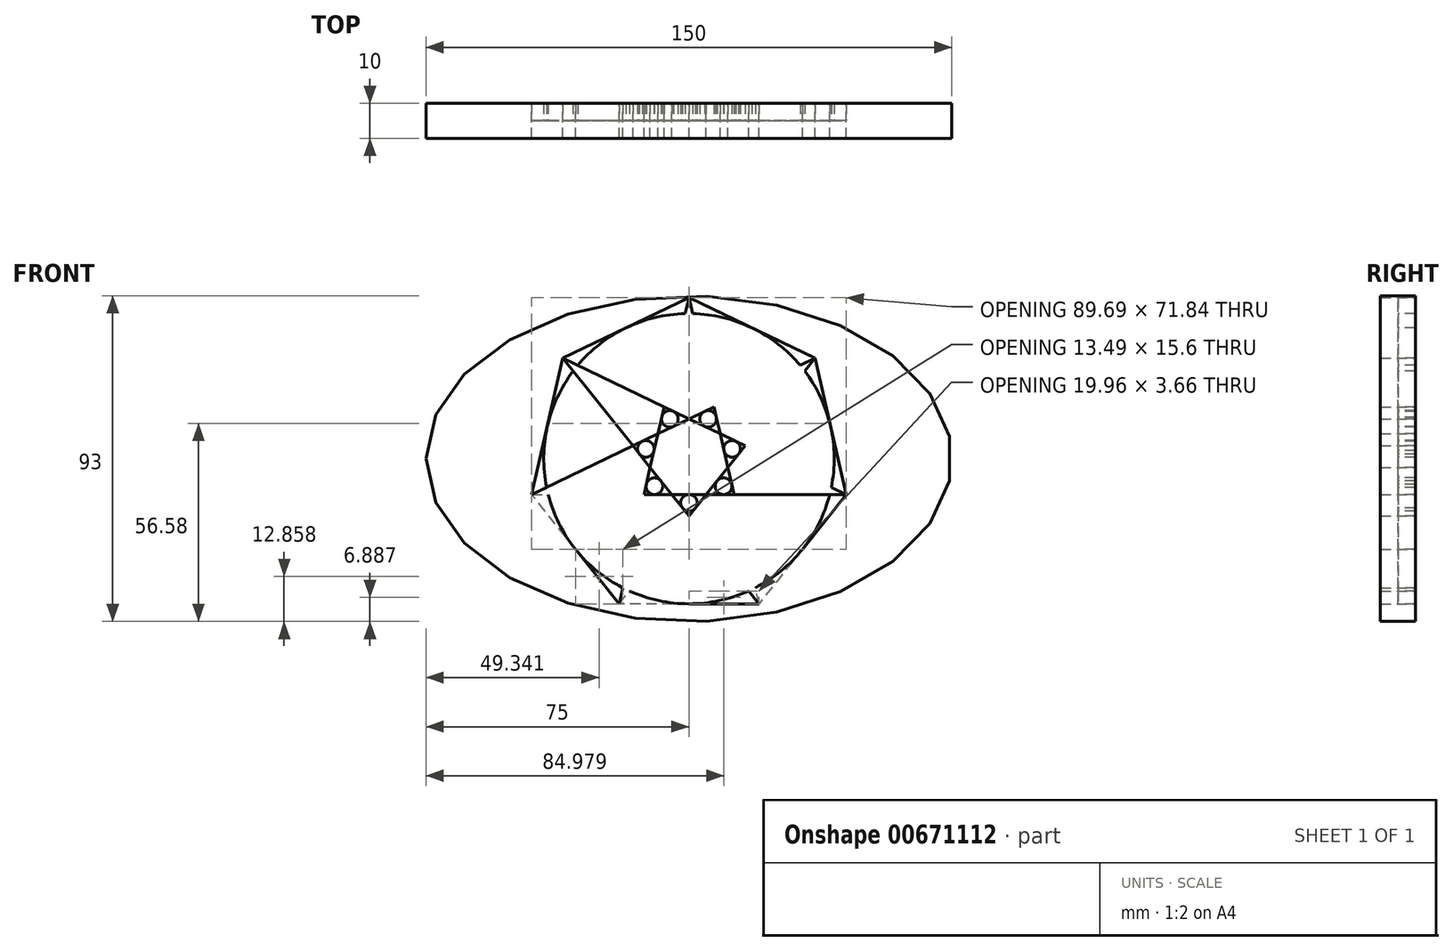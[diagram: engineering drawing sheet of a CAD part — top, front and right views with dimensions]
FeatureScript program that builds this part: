
annotation { "Feature Type Name" : "Feature", "Feature Type Description" : "" }
export const myFeature = defineFeature(function(context is Context, id is Id, definition is map)
    precondition{}
    {
        {
            var Q0;
            Q0=qCreatedBy(makeId("Front.planeOp"),FACE);
            var sketch = newSketch(context, id + "F0", { "sketchPlane" : qUnion([Q0])});
            skCircle(sketch, "E0", {"center": v(0, 0) * mm, "radius": 46 * mm});
            skEllipse(sketch, "E1", {"center": v(0, 0) * mm, "majorRadius": 75 * mm, "minorRadius": 46.5 * mm, "majorAxis": v(-1, 0)});
            skCircle(sketch, "E2.cCircle", {"center": v(0, 0) * mm, "radius": 46 * mm, "construction": true});
            skLineSegment(sketch, "E2.0", {"start": v(0, 46) * mm, "end": v(35.96, 28.68) * mm});
            skLineSegment(sketch, "E2.1", {"start": v(35.96, 28.68) * mm, "end": v(44.85, -10.24) * mm});
            skLineSegment(sketch, "E2.2", {"start": v(44.85, -10.24) * mm, "end": v(19.96, -41.44) * mm});
            skLineSegment(sketch, "E2.3", {"start": v(19.96, -41.44) * mm, "end": v(-19.96, -41.44) * mm});
            skLineSegment(sketch, "E2.4", {"start": v(-19.96, -41.44) * mm, "end": v(-44.85, -10.24) * mm});
            skLineSegment(sketch, "E2.5", {"start": v(-44.85, -10.24) * mm, "end": v(-35.96, 28.68) * mm});
            skLineSegment(sketch, "E2.6", {"start": v(-35.96, 28.68) * mm, "end": v(0, 46) * mm});
            skCircle(sketch, "E3", {"center": v(0, 0) * mm, "radius": 41.44 * mm});
            skLineSegment(sketch, "E4", {"start": v(-35.96, 28.68) * mm, "end": v(44.85, -10.24) * mm});
            skLineSegment(sketch, "E5", {"start": v(-35.96, 28.68) * mm, "end": v(19.96, -41.44) * mm});
            skLineSegment(sketch, "E6", {"start": v(19.96, -41.44) * mm, "end": v(0, 46) * mm});
            skLineSegment(sketch, "E7", {"start": v(-19.96, -41.44) * mm, "end": v(35.96, 28.68) * mm});
            skLineSegment(sketch, "E8", {"start": v(-44.85, -10.24) * mm, "end": v(44.85, -10.24) * mm});
            skLineSegment(sketch, "E9", {"start": v(0, 46) * mm, "end": v(-19.96, -41.44) * mm});
            skLineSegment(sketch, "E10", {"start": v(35.96, 28.68) * mm, "end": v(-44.85, -10.24) * mm});
            skPoint(sketch, "E11", {"position": v(-12.3, 2.8) * mm});
            skCircle(sketch, "E12", {"center": v(-12.3, 2.8) * mm, "radius": 2.37 * mm});
            skLineSegment(sketch, "E13", {"start": v(-16, 3.65) * mm, "end": v(-9.98, 2.28) * mm});
            skCircle(sketch, "E14.1.0", {"center": v(-9.86, -7.86) * mm, "radius": 2.37 * mm});
            skLineSegment(sketch, "E14.1.1", {"start": v(-12.84, -10.24) * mm, "end": v(-8, -6.38) * mm});
            skPoint(sketch, "E14.1.2", {"position": v(-9.86, -7.86) * mm});
            skCircle(sketch, "E14.2.0", {"center": v(0, -12.6) * mm, "radius": 2.37 * mm});
            skLineSegment(sketch, "E14.2.1", {"start": v(0, -16.42) * mm, "end": v(0, -10.24) * mm});
            skPoint(sketch, "E14.2.2", {"position": v(0, -12.6) * mm});
            skCircle(sketch, "E14.3.0", {"center": v(9.86, -7.86) * mm, "radius": 2.37 * mm});
            skLineSegment(sketch, "E14.3.1", {"start": v(12.84, -10.24) * mm, "end": v(8, -6.38) * mm});
            skPoint(sketch, "E14.3.2", {"position": v(9.86, -7.86) * mm});
            skCircle(sketch, "E14.4.0", {"center": v(12.3, 2.8) * mm, "radius": 2.37 * mm});
            skLineSegment(sketch, "E14.4.1", {"start": v(16, 3.65) * mm, "end": v(9.98, 2.28) * mm});
            skPoint(sketch, "E14.4.2", {"position": v(12.3, 2.8) * mm});
            skCircle(sketch, "E14.5.0", {"center": v(5.47, 11.36) * mm, "radius": 2.37 * mm});
            skLineSegment(sketch, "E14.5.1", {"start": v(7.12, 14.8) * mm, "end": v(4.44, 9.22) * mm});
            skPoint(sketch, "E14.5.2", {"position": v(5.47, 11.36) * mm});
            skCircle(sketch, "E14.6.0", {"center": v(-5.47, 11.36) * mm, "radius": 2.37 * mm});
            skLineSegment(sketch, "E14.6.1", {"start": v(-7.12, 14.8) * mm, "end": v(-4.44, 9.22) * mm});
            skPoint(sketch, "E14.6.2", {"position": v(-5.47, 11.36) * mm});
            skSolve(sketch);
        }
        {
            var Q0;
            {var subQ1=sQuery(id+"F0.wireOp",EDGE,"E4");var subQ7=sQuery(id+"F0.wireOp",EDGE,"E3");var subQ9=makeQuery(id+"F0.imprint","INTERSECT",VERTEX,{"disambiguationData":[OD(0.0)],"derivedFrom":[subQ7,subQ1]});Q0=makeQuery(id+"F0.imprint","IMPRINT",FACE,{"disambiguationData":[TD([[makeQuery(id+"F0.imprint","IMPRINT",EDGE,{"disambiguationData":[TD([[subQ9,-1.0]])],"derivedFrom":subQ7}),1.0]])]});}
            var Q1;
            {var subQ0=sQuery(id+"F0.wireOp",EDGE,"E4");var subQ1=sQuery(id+"F0.wireOp",EDGE,"E3");var subQ2=makeQuery(id+"F0.imprint","INTERSECT",VERTEX,{"disambiguationData":[OD(0.0)],"derivedFrom":[subQ1,subQ0]});Q1=makeQuery(id+"F0.imprint","IMPRINT",FACE,{"disambiguationData":[TD([[makeQuery(id+"F0.imprint","IMPRINT",EDGE,{"disambiguationData":[TD([[subQ2,-1.0]])],"derivedFrom":subQ1}),-1.0]])]});}
            var Q2;
            {var subQ3=sQuery(id+"F0.wireOp",EDGE,"E3");var subQ5=sQuery(id+"F0.wireOp",EDGE,"E10");var subQ6=makeQuery(id+"F0.imprint","INTERSECT",VERTEX,{"disambiguationData":[OD(1.0)],"derivedFrom":[subQ3,subQ5]});Q2=makeQuery(id+"F0.imprint","IMPRINT",FACE,{"disambiguationData":[TD([[makeQuery(id+"F0.imprint","IMPRINT",EDGE,{"disambiguationData":[TD([[subQ6,-1.0]])],"derivedFrom":subQ3}),1.0]])]});}
            var Q3;
            {var subQ0=sQuery(id+"F0.wireOp",EDGE,"E10");var subQ1=sQuery(id+"F0.wireOp",EDGE,"E3");var subQ2=makeQuery(id+"F0.imprint","INTERSECT",VERTEX,{"disambiguationData":[OD(1.0)],"derivedFrom":[subQ1,subQ0]});Q3=makeQuery(id+"F0.imprint","IMPRINT",FACE,{"disambiguationData":[TD([[makeQuery(id+"F0.imprint","IMPRINT",EDGE,{"disambiguationData":[TD([[subQ2,-1.0]])],"derivedFrom":subQ1}),-1.0]])]});}
            var Q4;
            {var subQ0=sQuery(id+"F0.wireOp",EDGE,"E9");var subQ7=sQuery(id+"F0.wireOp",EDGE,"E3");var subQ9=makeQuery(id+"F0.imprint","INTERSECT",VERTEX,{"disambiguationData":[OD(1.0)],"derivedFrom":[subQ7,subQ0]});Q4=makeQuery(id+"F0.imprint","IMPRINT",FACE,{"disambiguationData":[TD([[makeQuery(id+"F0.imprint","IMPRINT",EDGE,{"disambiguationData":[TD([[subQ9,-1.0]])],"derivedFrom":subQ7}),1.0]])]});}
            var Q5;
            {var subQ0=sQuery(id+"F0.wireOp",EDGE,"E9");var subQ1=sQuery(id+"F0.wireOp",EDGE,"E3");var subQ2=makeQuery(id+"F0.imprint","INTERSECT",VERTEX,{"disambiguationData":[OD(1.0)],"derivedFrom":[subQ1,subQ0]});Q5=makeQuery(id+"F0.imprint","IMPRINT",FACE,{"disambiguationData":[TD([[makeQuery(id+"F0.imprint","IMPRINT",EDGE,{"disambiguationData":[TD([[subQ2,-1.0]])],"derivedFrom":subQ1}),-1.0]])]});}
            var Q6;
            {var subQ1=sQuery(id+"F0.wireOp",EDGE,"E5");var subQ7=sQuery(id+"F0.wireOp",EDGE,"E3");var subQ9=makeQuery(id+"F0.imprint","INTERSECT",VERTEX,{"disambiguationData":[OD(1.0)],"derivedFrom":[subQ7,subQ1]});Q6=makeQuery(id+"F0.imprint","IMPRINT",FACE,{"disambiguationData":[TD([[makeQuery(id+"F0.imprint","IMPRINT",EDGE,{"disambiguationData":[TD([[subQ9,-1.0]])],"derivedFrom":subQ7}),1.0]])]});}
            var Q7;
            {var subQ0=sQuery(id+"F0.wireOp",EDGE,"E5");var subQ1=sQuery(id+"F0.wireOp",EDGE,"E3");var subQ2=makeQuery(id+"F0.imprint","INTERSECT",VERTEX,{"disambiguationData":[OD(1.0)],"derivedFrom":[subQ1,subQ0]});Q7=makeQuery(id+"F0.imprint","IMPRINT",FACE,{"disambiguationData":[TD([[makeQuery(id+"F0.imprint","IMPRINT",EDGE,{"disambiguationData":[TD([[subQ2,-1.0]])],"derivedFrom":subQ1}),-1.0]])]});}
            var Q8;
            {var subQ5=sQuery(id+"F0.wireOp",EDGE,"E8");var subQ7=sQuery(id+"F0.wireOp",EDGE,"E3");var subQ9=makeQuery(id+"F0.imprint","INTERSECT",VERTEX,{"disambiguationData":[OD(1.0)],"derivedFrom":[subQ7,subQ5]});Q8=makeQuery(id+"F0.imprint","IMPRINT",FACE,{"disambiguationData":[TD([[makeQuery(id+"F0.imprint","IMPRINT",EDGE,{"disambiguationData":[TD([[subQ9,-1.0]])],"derivedFrom":subQ7}),1.0]])]});}
            var Q9;
            {var subQ0=sQuery(id+"F0.wireOp",EDGE,"E8");var subQ1=sQuery(id+"F0.wireOp",EDGE,"E3");var subQ2=makeQuery(id+"F0.imprint","INTERSECT",VERTEX,{"disambiguationData":[OD(1.0)],"derivedFrom":[subQ1,subQ0]});Q9=makeQuery(id+"F0.imprint","IMPRINT",FACE,{"disambiguationData":[TD([[makeQuery(id+"F0.imprint","IMPRINT",EDGE,{"disambiguationData":[TD([[subQ2,-1.0]])],"derivedFrom":subQ1}),-1.0]])]});}
            var Q10;
            {var subQ5=sQuery(id+"F0.wireOp",EDGE,"E7");var subQ7=sQuery(id+"F0.wireOp",EDGE,"E3");var subQ8=makeQuery(id+"F0.imprint","INTERSECT",VERTEX,{"disambiguationData":[OD(0.0)],"derivedFrom":[subQ7,subQ5]});Q10=makeQuery(id+"F0.imprint","IMPRINT",FACE,{"disambiguationData":[TD([[makeQuery(id+"F0.imprint","IMPRINT",EDGE,{"disambiguationData":[TD([[subQ8,-1.0]])],"derivedFrom":subQ7}),1.0]])]});}
            var Q11;
            {var subQ0=sQuery(id+"F0.wireOp",EDGE,"E7");var subQ1=sQuery(id+"F0.wireOp",EDGE,"E3");var subQ2=makeQuery(id+"F0.imprint","INTERSECT",VERTEX,{"disambiguationData":[OD(0.0)],"derivedFrom":[subQ1,subQ0]});Q11=makeQuery(id+"F0.imprint","IMPRINT",FACE,{"disambiguationData":[TD([[makeQuery(id+"F0.imprint","IMPRINT",EDGE,{"disambiguationData":[TD([[subQ2,-1.0]])],"derivedFrom":subQ1}),-1.0]])]});}
            var Q12;
            {var subQ3=sQuery(id+"F0.wireOp",EDGE,"E3");var subQ6=sQuery(id+"F0.wireOp",EDGE,"E6");var subQ8=makeQuery(id+"F0.imprint","INTERSECT",VERTEX,{"disambiguationData":[OD(0.0)],"derivedFrom":[subQ3,subQ6]});Q12=makeQuery(id+"F0.imprint","IMPRINT",FACE,{"disambiguationData":[TD([[makeQuery(id+"F0.imprint","IMPRINT",EDGE,{"disambiguationData":[TD([[subQ8,-1.0]])],"derivedFrom":subQ3}),1.0]])]});}
            var Q13;
            {var subQ0=sQuery(id+"F0.wireOp",EDGE,"E6");var subQ1=sQuery(id+"F0.wireOp",EDGE,"E3");var subQ2=makeQuery(id+"F0.imprint","INTERSECT",VERTEX,{"disambiguationData":[OD(0.0)],"derivedFrom":[subQ1,subQ0]});Q13=makeQuery(id+"F0.imprint","IMPRINT",FACE,{"disambiguationData":[TD([[makeQuery(id+"F0.imprint","IMPRINT",EDGE,{"disambiguationData":[TD([[subQ2,-1.0]])],"derivedFrom":subQ1}),-1.0]])]});}
            var Q14;
            {var subQ0=sQuery(id+"F0.wireOp",EDGE,"3fb7257f-58bd-4f18-b406-dab5ca3c946f");Q14=makeQuery(id+"F0.imprint","IMPRINT",FACE,{"disambiguationData":[TD([[makeQuery(id+"F0.imprint","IMPRINT",EDGE,{"derivedFrom":subQ0}),1.0]])]});}
            var Q15;
            {var subQ0=sQuery(id+"F0.wireOp",EDGE,"b29785f3-1675-4353-98de-94516835d5aa.5.1");Q15=makeQuery(id+"F0.imprint","IMPRINT",FACE,{"disambiguationData":[TD([[makeQuery(id+"F0.imprint","IMPRINT",EDGE,{"derivedFrom":subQ0}),-1.0]])]});}
            var Q16;
            {var subQ4=sQuery(id+"F0.wireOp",EDGE,"b29785f3-1675-4353-98de-94516835d5aa.4.1");Q16=makeQuery(id+"F0.imprint","IMPRINT",FACE,{"disambiguationData":[TD([[makeQuery(id+"F0.imprint","IMPRINT",EDGE,{"derivedFrom":subQ4}),-1.0]])]});}
            var Q17;
            {var subQ4=sQuery(id+"F0.wireOp",EDGE,"b29785f3-1675-4353-98de-94516835d5aa.3.1");Q17=makeQuery(id+"F0.imprint","IMPRINT",FACE,{"disambiguationData":[TD([[makeQuery(id+"F0.imprint","IMPRINT",EDGE,{"derivedFrom":subQ4}),-1.0]])]});}
            var Q18;
            {var subQ4=sQuery(id+"F0.wireOp",EDGE,"b29785f3-1675-4353-98de-94516835d5aa.2.1");Q18=makeQuery(id+"F0.imprint","IMPRINT",FACE,{"disambiguationData":[TD([[makeQuery(id+"F0.imprint","IMPRINT",EDGE,{"derivedFrom":subQ4}),-1.0]])]});}
            var Q19;
            {var subQ0=sQuery(id+"F0.wireOp",EDGE,"b29785f3-1675-4353-98de-94516835d5aa.1.1");Q19=makeQuery(id+"F0.imprint","IMPRINT",FACE,{"disambiguationData":[TD([[makeQuery(id+"F0.imprint","IMPRINT",EDGE,{"derivedFrom":subQ0}),-1.0]])]});}
            var Q20;
            {var subQ4=sQuery(id+"F0.wireOp",EDGE,"3fb7257f-58bd-4f18-b406-dab5ca3c946f");Q20=makeQuery(id+"F0.imprint","IMPRINT",FACE,{"disambiguationData":[TD([[makeQuery(id+"F0.imprint","IMPRINT",EDGE,{"derivedFrom":subQ4}),-1.0]])]});}
            var Q21;
            Q21=makeQuery(id+"F0.imprint","IMPRINT",FACE,{"disambiguationData":[TD([[makeQuery(id+"F0.imprint","IMPRINT",EDGE,{"derivedFrom":sQuery(id+"F0.wireOp",EDGE,"E1")}),1.0]])]});
            var Q22;
            {var subQ0=sQuery(id+"F0.wireOp",EDGE,"E2.3");var subQ4=makeQuery(id+"F0.imprint","INTERSECT",VERTEX,{"derivedFrom":[subQ0,sQuery(id+"F0.wireOp",EDGE,"E3")]});Q22=makeQuery(id+"F0.imprint","IMPRINT",FACE,{"disambiguationData":[TD([[makeQuery(id+"F0.imprint","IMPRINT",EDGE,{"disambiguationData":[TD([[subQ4,1.0]])],"derivedFrom":subQ0}),1.0]])]});}
            var Q23;
            {var subQ0=sQuery(id+"F0.wireOp",EDGE,"E2.4");var subQ4=makeQuery(id+"F0.imprint","INTERSECT",VERTEX,{"derivedFrom":[subQ0,sQuery(id+"F0.wireOp",EDGE,"E3")]});Q23=makeQuery(id+"F0.imprint","IMPRINT",FACE,{"disambiguationData":[TD([[makeQuery(id+"F0.imprint","IMPRINT",EDGE,{"disambiguationData":[TD([[subQ4,1.0]])],"derivedFrom":subQ0}),1.0]])]});}
            var Q24;
            {var subQ0=sQuery(id+"F0.wireOp",EDGE,"E2.5");var subQ4=makeQuery(id+"F0.imprint","INTERSECT",VERTEX,{"derivedFrom":[subQ0,sQuery(id+"F0.wireOp",EDGE,"E3")]});Q24=makeQuery(id+"F0.imprint","IMPRINT",FACE,{"disambiguationData":[TD([[makeQuery(id+"F0.imprint","IMPRINT",EDGE,{"disambiguationData":[TD([[subQ4,1.0]])],"derivedFrom":subQ0}),1.0]])]});}
            var Q25;
            {var subQ0=sQuery(id+"F0.wireOp",EDGE,"E2.6");var subQ4=makeQuery(id+"F0.imprint","INTERSECT",VERTEX,{"derivedFrom":[subQ0,sQuery(id+"F0.wireOp",EDGE,"E3")]});Q25=makeQuery(id+"F0.imprint","IMPRINT",FACE,{"disambiguationData":[TD([[makeQuery(id+"F0.imprint","IMPRINT",EDGE,{"disambiguationData":[TD([[subQ4,1.0]])],"derivedFrom":subQ0}),1.0]])]});}
            var Q26;
            {var subQ0=sQuery(id+"F0.wireOp",EDGE,"E2.0");var subQ4=makeQuery(id+"F0.imprint","INTERSECT",VERTEX,{"derivedFrom":[subQ0,sQuery(id+"F0.wireOp",EDGE,"E3")]});Q26=makeQuery(id+"F0.imprint","IMPRINT",FACE,{"disambiguationData":[TD([[makeQuery(id+"F0.imprint","IMPRINT",EDGE,{"disambiguationData":[TD([[subQ4,1.0]])],"derivedFrom":subQ0}),1.0]])]});}
            var Q27;
            {var subQ0=sQuery(id+"F0.wireOp",EDGE,"E2.1");var subQ4=makeQuery(id+"F0.imprint","INTERSECT",VERTEX,{"derivedFrom":[subQ0,sQuery(id+"F0.wireOp",EDGE,"E3")]});Q27=makeQuery(id+"F0.imprint","IMPRINT",FACE,{"disambiguationData":[TD([[makeQuery(id+"F0.imprint","IMPRINT",EDGE,{"disambiguationData":[TD([[subQ4,1.0]])],"derivedFrom":subQ0}),1.0]])]});}
            var Q28;
            {var subQ0=sQuery(id+"F0.wireOp",EDGE,"E2.2");var subQ4=makeQuery(id+"F0.imprint","INTERSECT",VERTEX,{"derivedFrom":[subQ0,sQuery(id+"F0.wireOp",EDGE,"E3")]});Q28=makeQuery(id+"F0.imprint","IMPRINT",FACE,{"disambiguationData":[TD([[makeQuery(id+"F0.imprint","IMPRINT",EDGE,{"disambiguationData":[TD([[subQ4,1.0]])],"derivedFrom":subQ0}),1.0]])]});}
            var Q29;
            {var subQ10=sQuery(id+"F0.wireOp",EDGE,"E4");var subQ16=sQuery(id+"F0.wireOp",EDGE,"E10");var subQ17=makeQuery(id+"F0.imprint","INTERSECT",VERTEX,{"derivedFrom":[subQ10,subQ16]});Q29=makeQuery(id+"F0.imprint","IMPRINT",FACE,{"disambiguationData":[TD([[makeQuery(id+"F0.imprint","IMPRINT",EDGE,{"disambiguationData":[TD([[subQ17,-1.0]])],"derivedFrom":subQ10}),-1.0]])]});}
            extrude(context, id + "F1", {"entities" : qUnion([Q0, Q1, Q2, Q3, Q4, Q5, Q6, Q7, Q8, Q9, Q10, Q11, Q12, Q13, Q14, Q15, Q16, Q17, Q18, Q19, Q20, Q21, Q22, Q23, Q24, Q25, Q26, Q27, Q28, Q29]), "endBound" : BoundingType.SYMMETRIC, "depth" : 10 * mm, "offsetDistance" : 25 * mm});
        }
        {
            var Q0;
            {var subQ1=sQuery(id+"F0.wireOp",EDGE,"E2.5");var subQ3=sQuery(id+"F0.wireOp",EDGE,"E3");var subQ4=makeQuery(id+"F0.imprint","INTERSECT",VERTEX,{"derivedFrom":[subQ1,subQ3]});Q0=makeQuery(id+"F0.imprint","IMPRINT",FACE,{"disambiguationData":[TD([[makeQuery(id+"F0.imprint","IMPRINT",EDGE,{"disambiguationData":[TD([[subQ4,1.0]])],"derivedFrom":subQ3}),-1.0]])]});}
            var Q1;
            {var subQ1=sQuery(id+"F0.wireOp",EDGE,"E2.6");var subQ3=sQuery(id+"F0.wireOp",EDGE,"E3");var subQ4=makeQuery(id+"F0.imprint","INTERSECT",VERTEX,{"derivedFrom":[subQ1,subQ3]});Q1=makeQuery(id+"F0.imprint","IMPRINT",FACE,{"disambiguationData":[TD([[makeQuery(id+"F0.imprint","IMPRINT",EDGE,{"disambiguationData":[TD([[subQ4,-1.0]])],"derivedFrom":subQ3}),-1.0]])]});}
            var Q2;
            {var subQ1=sQuery(id+"F0.wireOp",EDGE,"E2.6");var subQ3=sQuery(id+"F0.wireOp",EDGE,"E3");var subQ4=makeQuery(id+"F0.imprint","INTERSECT",VERTEX,{"derivedFrom":[subQ1,subQ3]});Q2=makeQuery(id+"F0.imprint","IMPRINT",FACE,{"disambiguationData":[TD([[makeQuery(id+"F0.imprint","IMPRINT",EDGE,{"disambiguationData":[TD([[subQ4,1.0]])],"derivedFrom":subQ3}),-1.0]])]});}
            var Q3;
            {var subQ1=sQuery(id+"F0.wireOp",EDGE,"E2.0");var subQ3=sQuery(id+"F0.wireOp",EDGE,"E3");var subQ4=makeQuery(id+"F0.imprint","INTERSECT",VERTEX,{"derivedFrom":[subQ1,subQ3]});Q3=makeQuery(id+"F0.imprint","IMPRINT",FACE,{"disambiguationData":[TD([[makeQuery(id+"F0.imprint","IMPRINT",EDGE,{"disambiguationData":[TD([[subQ4,-1.0]])],"derivedFrom":subQ3}),-1.0]])]});}
            var Q4;
            {var subQ1=sQuery(id+"F0.wireOp",EDGE,"E2.0");var subQ3=sQuery(id+"F0.wireOp",EDGE,"E3");var subQ4=makeQuery(id+"F0.imprint","INTERSECT",VERTEX,{"derivedFrom":[subQ1,subQ3]});Q4=makeQuery(id+"F0.imprint","IMPRINT",FACE,{"disambiguationData":[TD([[makeQuery(id+"F0.imprint","IMPRINT",EDGE,{"disambiguationData":[TD([[subQ4,1.0]])],"derivedFrom":subQ3}),-1.0]])]});}
            var Q5;
            {var subQ1=sQuery(id+"F0.wireOp",EDGE,"E2.1");var subQ3=sQuery(id+"F0.wireOp",EDGE,"E3");var subQ4=makeQuery(id+"F0.imprint","INTERSECT",VERTEX,{"derivedFrom":[subQ1,subQ3]});Q5=makeQuery(id+"F0.imprint","IMPRINT",FACE,{"disambiguationData":[TD([[makeQuery(id+"F0.imprint","IMPRINT",EDGE,{"disambiguationData":[TD([[subQ4,-1.0]])],"derivedFrom":subQ3}),-1.0]])]});}
            var Q6;
            {var subQ1=sQuery(id+"F0.wireOp",EDGE,"E2.1");var subQ3=sQuery(id+"F0.wireOp",EDGE,"E3");var subQ4=makeQuery(id+"F0.imprint","INTERSECT",VERTEX,{"derivedFrom":[subQ1,subQ3]});Q6=makeQuery(id+"F0.imprint","IMPRINT",FACE,{"disambiguationData":[TD([[makeQuery(id+"F0.imprint","IMPRINT",EDGE,{"disambiguationData":[TD([[subQ4,1.0]])],"derivedFrom":subQ3}),-1.0]])]});}
            var Q7;
            {var subQ1=sQuery(id+"F0.wireOp",EDGE,"E2.2");var subQ3=sQuery(id+"F0.wireOp",EDGE,"E3");var subQ4=makeQuery(id+"F0.imprint","INTERSECT",VERTEX,{"derivedFrom":[subQ1,subQ3]});Q7=makeQuery(id+"F0.imprint","IMPRINT",FACE,{"disambiguationData":[TD([[makeQuery(id+"F0.imprint","IMPRINT",EDGE,{"disambiguationData":[TD([[subQ4,-1.0]])],"derivedFrom":subQ3}),-1.0]])]});}
            var Q8;
            {var subQ1=sQuery(id+"F0.wireOp",EDGE,"E2.2");var subQ3=sQuery(id+"F0.wireOp",EDGE,"E3");var subQ4=makeQuery(id+"F0.imprint","INTERSECT",VERTEX,{"derivedFrom":[subQ1,subQ3]});Q8=makeQuery(id+"F0.imprint","IMPRINT",FACE,{"disambiguationData":[TD([[makeQuery(id+"F0.imprint","IMPRINT",EDGE,{"disambiguationData":[TD([[subQ4,1.0]])],"derivedFrom":subQ3}),-1.0]])]});}
            var Q9;
            {var subQ1=sQuery(id+"F0.wireOp",EDGE,"E2.3");var subQ3=sQuery(id+"F0.wireOp",EDGE,"E3");var subQ4=makeQuery(id+"F0.imprint","INTERSECT",VERTEX,{"derivedFrom":[subQ1,subQ3]});Q9=makeQuery(id+"F0.imprint","IMPRINT",FACE,{"disambiguationData":[TD([[makeQuery(id+"F0.imprint","IMPRINT",EDGE,{"disambiguationData":[TD([[subQ4,-1.0]])],"derivedFrom":subQ3}),-1.0]])]});}
            var Q10;
            {var subQ1=sQuery(id+"F0.wireOp",EDGE,"E2.3");var subQ3=sQuery(id+"F0.wireOp",EDGE,"E3");var subQ4=makeQuery(id+"F0.imprint","INTERSECT",VERTEX,{"derivedFrom":[subQ1,subQ3]});Q10=makeQuery(id+"F0.imprint","IMPRINT",FACE,{"disambiguationData":[TD([[makeQuery(id+"F0.imprint","IMPRINT",EDGE,{"disambiguationData":[TD([[subQ4,1.0]])],"derivedFrom":subQ3}),-1.0]])]});}
            var Q11;
            {var subQ1=sQuery(id+"F0.wireOp",EDGE,"E2.4");var subQ3=sQuery(id+"F0.wireOp",EDGE,"E3");var subQ4=makeQuery(id+"F0.imprint","INTERSECT",VERTEX,{"derivedFrom":[subQ1,subQ3]});Q11=makeQuery(id+"F0.imprint","IMPRINT",FACE,{"disambiguationData":[TD([[makeQuery(id+"F0.imprint","IMPRINT",EDGE,{"disambiguationData":[TD([[subQ4,-1.0]])],"derivedFrom":subQ3}),-1.0]])]});}
            var Q12;
            {var subQ1=sQuery(id+"F0.wireOp",EDGE,"E2.4");var subQ3=sQuery(id+"F0.wireOp",EDGE,"E3");var subQ4=makeQuery(id+"F0.imprint","INTERSECT",VERTEX,{"derivedFrom":[subQ1,subQ3]});Q12=makeQuery(id+"F0.imprint","IMPRINT",FACE,{"disambiguationData":[TD([[makeQuery(id+"F0.imprint","IMPRINT",EDGE,{"disambiguationData":[TD([[subQ4,1.0]])],"derivedFrom":subQ3}),-1.0]])]});}
            var Q13;
            {var subQ1=sQuery(id+"F0.wireOp",EDGE,"E2.5");var subQ3=sQuery(id+"F0.wireOp",EDGE,"E3");var subQ4=makeQuery(id+"F0.imprint","INTERSECT",VERTEX,{"derivedFrom":[subQ1,subQ3]});Q13=makeQuery(id+"F0.imprint","IMPRINT",FACE,{"disambiguationData":[TD([[makeQuery(id+"F0.imprint","IMPRINT",EDGE,{"disambiguationData":[TD([[subQ4,-1.0]])],"derivedFrom":subQ3}),-1.0]])]});}
            var Q14;
            {var subQ0=sQuery(id+"F0.wireOp",EDGE,"E14.6.0");var subQ1=sQuery(id+"F0.wireOp",EDGE,"E9");var subQ2=makeQuery(id+"F0.imprint","INTERSECT",VERTEX,{"derivedFrom":[subQ1,subQ0]});Q14=makeQuery(id+"F0.imprint","IMPRINT",FACE,{"disambiguationData":[TD([[makeQuery(id+"F0.imprint","IMPRINT",EDGE,{"disambiguationData":[TD([[subQ2,-1.0]])],"derivedFrom":subQ1}),1.0]])]});}
            var Q15;
            {var subQ1=sQuery(id+"F0.wireOp",EDGE,"E9");var subQ3=sQuery(id+"F0.wireOp",EDGE,"E14.6.0");var subQ4=makeQuery(id+"F0.imprint","INTERSECT",VERTEX,{"derivedFrom":[subQ1,subQ3]});Q15=makeQuery(id+"F0.imprint","IMPRINT",FACE,{"disambiguationData":[TD([[makeQuery(id+"F0.imprint","IMPRINT",EDGE,{"disambiguationData":[TD([[subQ4,1.0]])],"derivedFrom":subQ3}),-1.0]])]});}
            var Q16;
            {var subQ1=sQuery(id+"F0.wireOp",EDGE,"E4");var subQ3=sQuery(id+"F0.wireOp",EDGE,"E14.6.0");var subQ4=makeQuery(id+"F0.imprint","INTERSECT",VERTEX,{"derivedFrom":[subQ1,subQ3]});Q16=makeQuery(id+"F0.imprint","IMPRINT",FACE,{"disambiguationData":[TD([[makeQuery(id+"F0.imprint","IMPRINT",EDGE,{"disambiguationData":[TD([[subQ4,-1.0]])],"derivedFrom":subQ3}),-1.0]])]});}
            var Q17;
            {var subQ0=sQuery(id+"F0.wireOp",EDGE,"E14.6.0");var subQ1=sQuery(id+"F0.wireOp",EDGE,"E4");var subQ2=makeQuery(id+"F0.imprint","INTERSECT",VERTEX,{"derivedFrom":[subQ1,subQ0]});Q17=makeQuery(id+"F0.imprint","IMPRINT",FACE,{"disambiguationData":[TD([[makeQuery(id+"F0.imprint","IMPRINT",EDGE,{"disambiguationData":[TD([[subQ2,-1.0]])],"derivedFrom":subQ1}),-1.0]])]});}
            var Q18;
            {var subQ1=sQuery(id+"F0.wireOp",EDGE,"E6");var subQ3=sQuery(id+"F0.wireOp",EDGE,"E14.5.0");var subQ4=makeQuery(id+"F0.imprint","INTERSECT",VERTEX,{"derivedFrom":[subQ1,subQ3]});Q18=makeQuery(id+"F0.imprint","IMPRINT",FACE,{"disambiguationData":[TD([[makeQuery(id+"F0.imprint","IMPRINT",EDGE,{"disambiguationData":[TD([[subQ4,-1.0]])],"derivedFrom":subQ3}),-1.0]])]});}
            var Q19;
            {var subQ1=sQuery(id+"F0.wireOp",EDGE,"E4");var subQ3=sQuery(id+"F0.wireOp",EDGE,"E6");var subQ4=makeQuery(id+"F0.imprint","INTERSECT",VERTEX,{"derivedFrom":[subQ1,subQ3]});Q19=makeQuery(id+"F0.imprint","IMPRINT",FACE,{"disambiguationData":[TD([[makeQuery(id+"F0.imprint","IMPRINT",EDGE,{"disambiguationData":[TD([[subQ4,-1.0]])],"derivedFrom":subQ3}),1.0]])]});}
            var Q20;
            {var subQ0=sQuery(id+"F0.wireOp",EDGE,"E6");var subQ1=sQuery(id+"F0.wireOp",EDGE,"E4");var subQ2=makeQuery(id+"F0.imprint","INTERSECT",VERTEX,{"derivedFrom":[subQ1,subQ0]});Q20=makeQuery(id+"F0.imprint","IMPRINT",FACE,{"disambiguationData":[TD([[makeQuery(id+"F0.imprint","IMPRINT",EDGE,{"disambiguationData":[TD([[subQ2,-1.0]])],"derivedFrom":subQ1}),-1.0]])]});}
            var Q21;
            {var subQ1=sQuery(id+"F0.wireOp",EDGE,"E4");var subQ3=sQuery(id+"F0.wireOp",EDGE,"E10");var subQ4=makeQuery(id+"F0.imprint","INTERSECT",VERTEX,{"derivedFrom":[subQ1,subQ3]});Q21=makeQuery(id+"F0.imprint","IMPRINT",FACE,{"disambiguationData":[TD([[makeQuery(id+"F0.imprint","IMPRINT",EDGE,{"disambiguationData":[TD([[subQ4,1.0]])],"derivedFrom":subQ3}),1.0]])]});}
            var Q22;
            {var subQ1=sQuery(id+"F0.wireOp",EDGE,"E10");var subQ3=sQuery(id+"F0.wireOp",EDGE,"E14.5.0");var subQ4=makeQuery(id+"F0.imprint","INTERSECT",VERTEX,{"derivedFrom":[subQ1,subQ3]});Q22=makeQuery(id+"F0.imprint","IMPRINT",FACE,{"disambiguationData":[TD([[makeQuery(id+"F0.imprint","IMPRINT",EDGE,{"disambiguationData":[TD([[subQ4,1.0]])],"derivedFrom":subQ3}),-1.0]])]});}
            var Q23;
            {var subQ1=sQuery(id+"F0.wireOp",EDGE,"E4");var subQ3=sQuery(id+"F0.wireOp",EDGE,"E14.4.0");var subQ4=makeQuery(id+"F0.imprint","INTERSECT",VERTEX,{"derivedFrom":[subQ1,subQ3]});Q23=makeQuery(id+"F0.imprint","IMPRINT",FACE,{"disambiguationData":[TD([[makeQuery(id+"F0.imprint","IMPRINT",EDGE,{"disambiguationData":[TD([[subQ4,1.0]])],"derivedFrom":subQ3}),-1.0]])]});}
            var Q24;
            {var subQ1=sQuery(id+"F0.wireOp",EDGE,"E7");var subQ3=sQuery(id+"F0.wireOp",EDGE,"E14.4.0");var subQ4=makeQuery(id+"F0.imprint","INTERSECT",VERTEX,{"derivedFrom":[subQ1,subQ3]});Q24=makeQuery(id+"F0.imprint","IMPRINT",FACE,{"disambiguationData":[TD([[makeQuery(id+"F0.imprint","IMPRINT",EDGE,{"disambiguationData":[TD([[subQ4,-1.0]])],"derivedFrom":subQ3}),-1.0]])]});}
            var Q25;
            {var subQ1=sQuery(id+"F0.wireOp",EDGE,"E6");var subQ3=sQuery(id+"F0.wireOp",EDGE,"E7");var subQ4=makeQuery(id+"F0.imprint","INTERSECT",VERTEX,{"derivedFrom":[subQ1,subQ3]});Q25=makeQuery(id+"F0.imprint","IMPRINT",FACE,{"disambiguationData":[TD([[makeQuery(id+"F0.imprint","IMPRINT",EDGE,{"disambiguationData":[TD([[subQ4,-1.0]])],"derivedFrom":subQ3}),1.0]])]});}
            var Q26;
            {var subQ0=sQuery(id+"F0.wireOp",EDGE,"E14.3.0");var subQ1=sQuery(id+"F0.wireOp",EDGE,"E6");var subQ2=makeQuery(id+"F0.imprint","INTERSECT",VERTEX,{"derivedFrom":[subQ1,subQ0]});Q26=makeQuery(id+"F0.imprint","IMPRINT",FACE,{"disambiguationData":[TD([[makeQuery(id+"F0.imprint","IMPRINT",EDGE,{"disambiguationData":[TD([[subQ2,-1.0]])],"derivedFrom":subQ1}),1.0]])]});}
            var Q27;
            {var subQ1=sQuery(id+"F0.wireOp",EDGE,"E6");var subQ3=sQuery(id+"F0.wireOp",EDGE,"E14.3.0");var subQ4=makeQuery(id+"F0.imprint","INTERSECT",VERTEX,{"derivedFrom":[subQ1,subQ3]});Q27=makeQuery(id+"F0.imprint","IMPRINT",FACE,{"disambiguationData":[TD([[makeQuery(id+"F0.imprint","IMPRINT",EDGE,{"disambiguationData":[TD([[subQ4,1.0]])],"derivedFrom":subQ3}),-1.0]])]});}
            var Q28;
            {var subQ1=sQuery(id+"F0.wireOp",EDGE,"E8");var subQ3=sQuery(id+"F0.wireOp",EDGE,"E14.3.0");var subQ4=makeQuery(id+"F0.imprint","INTERSECT",VERTEX,{"derivedFrom":[subQ1,subQ3]});Q28=makeQuery(id+"F0.imprint","IMPRINT",FACE,{"disambiguationData":[TD([[makeQuery(id+"F0.imprint","IMPRINT",EDGE,{"disambiguationData":[TD([[subQ4,-1.0]])],"derivedFrom":subQ3}),-1.0]])]});}
            var Q29;
            {var subQ1=sQuery(id+"F0.wireOp",EDGE,"E7");var subQ3=sQuery(id+"F0.wireOp",EDGE,"E8");var subQ4=makeQuery(id+"F0.imprint","INTERSECT",VERTEX,{"derivedFrom":[subQ1,subQ3]});Q29=makeQuery(id+"F0.imprint","IMPRINT",FACE,{"disambiguationData":[TD([[makeQuery(id+"F0.imprint","IMPRINT",EDGE,{"disambiguationData":[TD([[subQ4,-1.0]])],"derivedFrom":subQ3}),1.0]])]});}
            var Q30;
            {var subQ0=sQuery(id+"F0.wireOp",EDGE,"E14.2.0");var subQ1=sQuery(id+"F0.wireOp",EDGE,"E7");var subQ2=makeQuery(id+"F0.imprint","INTERSECT",VERTEX,{"derivedFrom":[subQ1,subQ0]});Q30=makeQuery(id+"F0.imprint","IMPRINT",FACE,{"disambiguationData":[TD([[makeQuery(id+"F0.imprint","IMPRINT",EDGE,{"disambiguationData":[TD([[subQ2,-1.0]])],"derivedFrom":subQ1}),1.0]])]});}
            var Q31;
            {var subQ0=sQuery(id+"F0.wireOp",EDGE,"E8");var subQ1=sQuery(id+"F0.wireOp",EDGE,"E5");var subQ2=makeQuery(id+"F0.imprint","INTERSECT",VERTEX,{"derivedFrom":[subQ1,subQ0]});Q31=makeQuery(id+"F0.imprint","IMPRINT",FACE,{"disambiguationData":[TD([[makeQuery(id+"F0.imprint","IMPRINT",EDGE,{"disambiguationData":[TD([[subQ2,-1.0]])],"derivedFrom":subQ1}),1.0]])]});}
            var Q32;
            {var subQ1=sQuery(id+"F0.wireOp",EDGE,"E5");var subQ3=sQuery(id+"F0.wireOp",EDGE,"E14.2.0");var subQ4=makeQuery(id+"F0.imprint","INTERSECT",VERTEX,{"derivedFrom":[subQ1,subQ3]});Q32=makeQuery(id+"F0.imprint","IMPRINT",FACE,{"disambiguationData":[TD([[makeQuery(id+"F0.imprint","IMPRINT",EDGE,{"disambiguationData":[TD([[subQ4,-1.0]])],"derivedFrom":subQ3}),-1.0]])]});}
            var Q33;
            {var subQ1=sQuery(id+"F0.wireOp",EDGE,"E7");var subQ3=sQuery(id+"F0.wireOp",EDGE,"E14.2.0");var subQ4=makeQuery(id+"F0.imprint","INTERSECT",VERTEX,{"derivedFrom":[subQ1,subQ3]});Q33=makeQuery(id+"F0.imprint","IMPRINT",FACE,{"disambiguationData":[TD([[makeQuery(id+"F0.imprint","IMPRINT",EDGE,{"disambiguationData":[TD([[subQ4,1.0]])],"derivedFrom":subQ3}),-1.0]])]});}
            var Q34;
            {var subQ1=sQuery(id+"F0.wireOp",EDGE,"E5");var subQ3=sQuery(id+"F0.wireOp",EDGE,"E8");var subQ4=makeQuery(id+"F0.imprint","INTERSECT",VERTEX,{"derivedFrom":[subQ1,subQ3]});Q34=makeQuery(id+"F0.imprint","IMPRINT",FACE,{"disambiguationData":[TD([[makeQuery(id+"F0.imprint","IMPRINT",EDGE,{"disambiguationData":[TD([[subQ4,1.0]])],"derivedFrom":subQ3}),1.0]])]});}
            var Q35;
            {var subQ1=sQuery(id+"F0.wireOp",EDGE,"E5");var subQ3=sQuery(id+"F0.wireOp",EDGE,"E9");var subQ4=makeQuery(id+"F0.imprint","INTERSECT",VERTEX,{"derivedFrom":[subQ1,subQ3]});Q35=makeQuery(id+"F0.imprint","IMPRINT",FACE,{"disambiguationData":[TD([[makeQuery(id+"F0.imprint","IMPRINT",EDGE,{"disambiguationData":[TD([[subQ4,-1.0]])],"derivedFrom":subQ3}),1.0]])]});}
            var Q36;
            {var subQ1=sQuery(id+"F0.wireOp",EDGE,"E9");var subQ3=sQuery(id+"F0.wireOp",EDGE,"E14.1.0");var subQ4=makeQuery(id+"F0.imprint","INTERSECT",VERTEX,{"derivedFrom":[subQ1,subQ3]});Q36=makeQuery(id+"F0.imprint","IMPRINT",FACE,{"disambiguationData":[TD([[makeQuery(id+"F0.imprint","IMPRINT",EDGE,{"disambiguationData":[TD([[subQ4,-1.0]])],"derivedFrom":subQ3}),-1.0]])]});}
            var Q37;
            {var subQ1=sQuery(id+"F0.wireOp",EDGE,"E8");var subQ3=sQuery(id+"F0.wireOp",EDGE,"E14.1.0");var subQ4=makeQuery(id+"F0.imprint","INTERSECT",VERTEX,{"derivedFrom":[subQ1,subQ3]});Q37=makeQuery(id+"F0.imprint","IMPRINT",FACE,{"disambiguationData":[TD([[makeQuery(id+"F0.imprint","IMPRINT",EDGE,{"disambiguationData":[TD([[subQ4,1.0]])],"derivedFrom":subQ3}),-1.0]])]});}
            var Q38;
            {var subQ0=sQuery(id+"F0.wireOp",EDGE,"E12");var subQ1=sQuery(id+"F0.wireOp",EDGE,"E5");var subQ2=makeQuery(id+"F0.imprint","INTERSECT",VERTEX,{"derivedFrom":[subQ1,subQ0]});Q38=makeQuery(id+"F0.imprint","IMPRINT",FACE,{"disambiguationData":[TD([[makeQuery(id+"F0.imprint","IMPRINT",EDGE,{"disambiguationData":[TD([[subQ2,-1.0]])],"derivedFrom":subQ1}),1.0]])]});}
            var Q39;
            {var subQ1=sQuery(id+"F0.wireOp",EDGE,"E9");var subQ3=sQuery(id+"F0.wireOp",EDGE,"E10");var subQ4=makeQuery(id+"F0.imprint","INTERSECT",VERTEX,{"derivedFrom":[subQ1,subQ3]});Q39=makeQuery(id+"F0.imprint","IMPRINT",FACE,{"disambiguationData":[TD([[makeQuery(id+"F0.imprint","IMPRINT",EDGE,{"disambiguationData":[TD([[subQ4,-1.0]])],"derivedFrom":subQ3}),1.0]])]});}
            var Q40;
            {var subQ1=sQuery(id+"F0.wireOp",EDGE,"E10");var subQ3=sQuery(id+"F0.wireOp",EDGE,"E12");var subQ4=makeQuery(id+"F0.imprint","INTERSECT",VERTEX,{"derivedFrom":[subQ1,subQ3]});Q40=makeQuery(id+"F0.imprint","IMPRINT",FACE,{"disambiguationData":[TD([[makeQuery(id+"F0.imprint","IMPRINT",EDGE,{"disambiguationData":[TD([[subQ4,-1.0]])],"derivedFrom":subQ3}),-1.0]])]});}
            var Q41;
            {var subQ1=sQuery(id+"F0.wireOp",EDGE,"E5");var subQ3=sQuery(id+"F0.wireOp",EDGE,"E12");var subQ4=makeQuery(id+"F0.imprint","INTERSECT",VERTEX,{"derivedFrom":[subQ1,subQ3]});Q41=makeQuery(id+"F0.imprint","IMPRINT",FACE,{"disambiguationData":[TD([[makeQuery(id+"F0.imprint","IMPRINT",EDGE,{"disambiguationData":[TD([[subQ4,1.0]])],"derivedFrom":subQ3}),-1.0]])]});}
            extrude(context, id + "F2", {"entities" : qUnion([Q0, Q1, Q2, Q3, Q4, Q5, Q6, Q7, Q8, Q9, Q10, Q11, Q12, Q13, Q14, Q15, Q16, Q17, Q18, Q19, Q20, Q21, Q22, Q23, Q24, Q25, Q26, Q27, Q28, Q29, Q30, Q31, Q32, Q33, Q34, Q35, Q36, Q37, Q38, Q39, Q40, Q41]), "oppositeDirection" : true, "depth" : 5 * mm, "offsetDistance" : 25 * mm});
        }
    });
